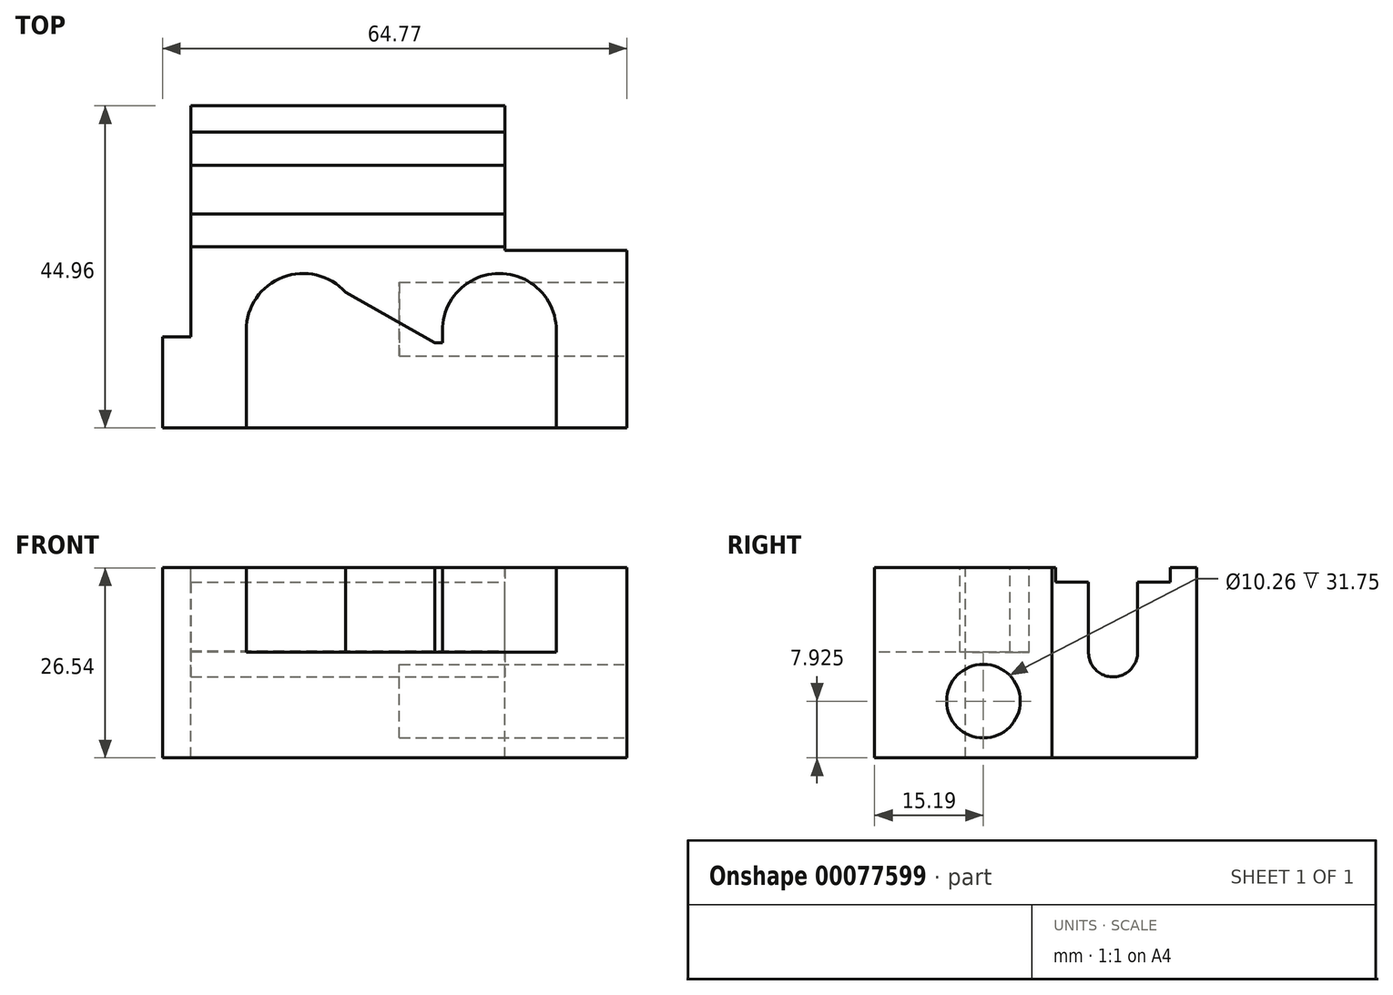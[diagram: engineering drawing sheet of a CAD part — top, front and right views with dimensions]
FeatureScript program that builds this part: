
annotation { "Feature Type Name" : "Feature", "Feature Type Description" : "" }
export const myFeature = defineFeature(function(context is Context, id is Id, definition is map)
    precondition{}
    {
        {
            var Q0;
            Q0=qCreatedBy(makeId("Top.planeOp"),FACE);
            var sketch = newSketch(context, id + "F0", { "sketchPlane" : qUnion([Q0])});
            skLineSegment(sketch, "E0.bottom", {"start": v(32.39, 22.48) * mm, "end": v(-32.39, 22.48) * mm});
            skLineSegment(sketch, "E0.top", {"start": v(32.39, -22.48) * mm, "end": v(-32.39, -22.48) * mm});
            skLineSegment(sketch, "E0.left", {"start": v(32.39, 22.48) * mm, "end": v(32.39, -22.48) * mm});
            skLineSegment(sketch, "E0.right", {"start": v(-32.39, 22.48) * mm, "end": v(-32.39, -22.48) * mm});
            skPoint(sketch, "E0.middle", {"position": v(0, 0) * mm});
            skSolve(sketch);
        }
        {
            var Q0;
            Q0 = qSketchRegion(id + "F0", true);
            extrude(context, id + "F1", {"entities" : qUnion([Q0]), "depth" : 26.54 * mm});
        }
        {
            var Q0;
            Q0=makeQuery(id+"F1.opExtrude","CAP_FACE",FACE,{"disambiguationData":[OSD([sQuery(id+"F0.wireOp",EDGE,"E0.bottom"),sQuery(id+"F0.wireOp",EDGE,"E0.top"),sQuery(id+"F0.wireOp",EDGE,"E0.left"),sQuery(id+"F0.wireOp",EDGE,"E0.right")])],"isStart":false});
            var sketch = newSketch(context, id + "F2", { "sketchPlane" : qUnion([Q0])});
            skLineSegment(sketch, "E1.bottom", {"start": v(-32.39, 22.48) * mm, "end": v(-28.42, 22.48) * mm});
            skLineSegment(sketch, "E1.top", {"start": v(-32.39, -9.78) * mm, "end": v(-28.42, -9.78) * mm});
            skLineSegment(sketch, "E1.left", {"start": v(-32.39, 22.48) * mm, "end": v(-32.39, -9.78) * mm});
            skLineSegment(sketch, "E1.right", {"start": v(-28.42, 22.48) * mm, "end": v(-28.42, -9.78) * mm});
            skLineSegment(sketch, "E2.bottom", {"start": v(32.39, 22.48) * mm, "end": v(15.37, 22.48) * mm});
            skLineSegment(sketch, "E2.top", {"start": v(32.39, 2.29) * mm, "end": v(15.37, 2.29) * mm});
            skLineSegment(sketch, "E2.left", {"start": v(32.39, 22.48) * mm, "end": v(32.39, 2.29) * mm});
            skLineSegment(sketch, "E2.right", {"start": v(15.37, 22.48) * mm, "end": v(15.37, 2.29) * mm});
            skSolve(sketch);
        }
        {
            var Q0;
            Q0 = qSketchRegion(id + "F2", true);
            extrude(context, id + "F3", {"entities" : qUnion([Q0]), "operationType" : NewBodyOperationType.REMOVE, "endBound" : BoundingType.THROUGH_ALL, "oppositeDirection" : true, "depth" : 25.4 * mm});
        }
        {
            var Q0;
            Q0=makeQuery(id+"F3.boolean.opBoolean","COPY",FACE,{"derivedFrom":makeQuery(id+"F3.opExtrude","SWEPT_FACE",FACE,{"disambiguationData":[OSD([sQuery(id+"F2.wireOp",EDGE,"E2.right")])]})});
            var sketch = newSketch(context, id + "F4", { "sketchPlane" : qUnion([Q0])});
            skArc(sketch, "E3", {"start": v(7.37, 14.85) * mm, "mid": v(10.84, 11.3) * mm, "end": v(14.22, 14.94) * mm});
            skLineSegment(sketch, "E4", {"start": v(14.22, 14.94) * mm, "end": v(14.22, 26.54) * mm});
            skLineSegment(sketch, "E5", {"start": v(7.37, 14.85) * mm, "end": v(7.37, 26.54) * mm});
            skLineSegment(sketch, "E6", {"start": v(7.37, 26.54) * mm, "end": v(14.22, 26.54) * mm});
            skLineSegment(sketch, "E7.bottom", {"start": v(18.8, 28.58) * mm, "end": v(2.8, 28.58) * mm});
            skLineSegment(sketch, "E7.top", {"start": v(18.8, 24.51) * mm, "end": v(2.8, 24.51) * mm});
            skLineSegment(sketch, "E7.left", {"start": v(18.8, 28.58) * mm, "end": v(18.8, 24.51) * mm});
            skLineSegment(sketch, "E7.right", {"start": v(2.8, 28.58) * mm, "end": v(2.8, 24.51) * mm});
            skPoint(sketch, "E7.middle", {"position": v(10.8, 26.54) * mm});
            skSolve(sketch);
        }
        {
            var Q0;
            Q0 = qSketchRegion(id + "F4", true);
            extrude(context, id + "F5", {"entities" : qUnion([Q0]), "operationType" : NewBodyOperationType.REMOVE, "endBound" : BoundingType.THROUGH_ALL, "oppositeDirection" : true, "depth" : 25.4 * mm});
        }
        {
            var Q0;
            {var subQ0=sQuery(id+"F0.wireOp",EDGE,"E0.right");var subQ1=sQuery(id+"F0.wireOp",EDGE,"E0.left");var subQ2=sQuery(id+"F0.wireOp",EDGE,"E0.top");Q0=makeQuery(id+"F5.boolean.opBoolean","SPLIT",FACE,{"disambiguationData":[TD([makeQuery(id+"F1.opExtrude","SWEPT_FACE",FACE,{"disambiguationData":[OSD([subQ2])]})])],"derivedFrom":makeQuery(id+"F1.opExtrude","CAP_FACE",FACE,{"disambiguationData":[OSD([sQuery(id+"F0.wireOp",EDGE,"E0.bottom"),subQ2,subQ1,subQ0])],"isStart":false})});}
            var sketch = newSketch(context, id + "F6", { "sketchPlane" : qUnion([Q0])});
            skArc(sketch, "E8", {"start": v(22.54, -8.84) * mm, "mid": v(14.57, -0.9) * mm, "end": v(6.67, -8.9) * mm});
            skArc(sketch, "E9", {"start": v(-6.85, -3.56) * mm, "mid": v(-15.6, -1.42) * mm, "end": v(-20.71, -8.84) * mm});
            skLineSegment(sketch, "E10", {"start": v(22.54, -8.84) * mm, "end": v(22.54, -22.48) * mm});
            skLineSegment(sketch, "E11", {"start": v(-20.71, -8.84) * mm, "end": v(-20.71, -22.48) * mm});
            skLineSegment(sketch, "E12", {"start": v(-6.85, -3.56) * mm, "end": v(5.6, -10.57) * mm});
            skLineSegment(sketch, "E13", {"start": v(5.6, -10.57) * mm, "end": v(6.67, -10.57) * mm});
            skLineSegment(sketch, "E14", {"start": v(6.67, -8.9) * mm, "end": v(6.67, -10.57) * mm});
            skPoint(sketch, "E15.orphan", {"position": v(6.86, -10.57) * mm});
            skSolve(sketch);
        }
        {
            var Q0;
            Q0 = qSketchRegion(id + "F6", true);
            var Q1;
            Q1=makeQuery(id+"F6.imprint","IMPRINT",FACE,{"disambiguationData":[TD([[makeQuery(id+"F6.imprint","IMPRINT",EDGE,{"derivedFrom":sQuery(id+"F6.wireOp",EDGE,"E8")}),1.0]])]});
            extrude(context, id + "F7", {"entities" : qUnion([Q0, Q1]), "operationType" : NewBodyOperationType.REMOVE, "oppositeDirection" : true, "depth" : 11.79 * mm});
        }
        {
            var Q0;
            Q0=makeQuery(id+"F1.opExtrude","SWEPT_FACE",FACE,{"disambiguationData":[OSD([sQuery(id+"F0.wireOp",EDGE,"E0.left")])]});
            var sketch = newSketch(context, id + "F8", { "sketchPlane" : qUnion([Q0])});
            skCircle(sketch, "E16", {"center": v(-7.29, 7.92) * mm, "radius": 5.13 * mm});
            skSolve(sketch);
        }
        {
            var Q0;
            Q0 = qSketchRegion(id + "F8", true);
            extrude(context, id + "F9", {"entities" : qUnion([Q0]), "operationType" : NewBodyOperationType.REMOVE, "oppositeDirection" : true, "depth" : 31.75 * mm});
        }
    });
